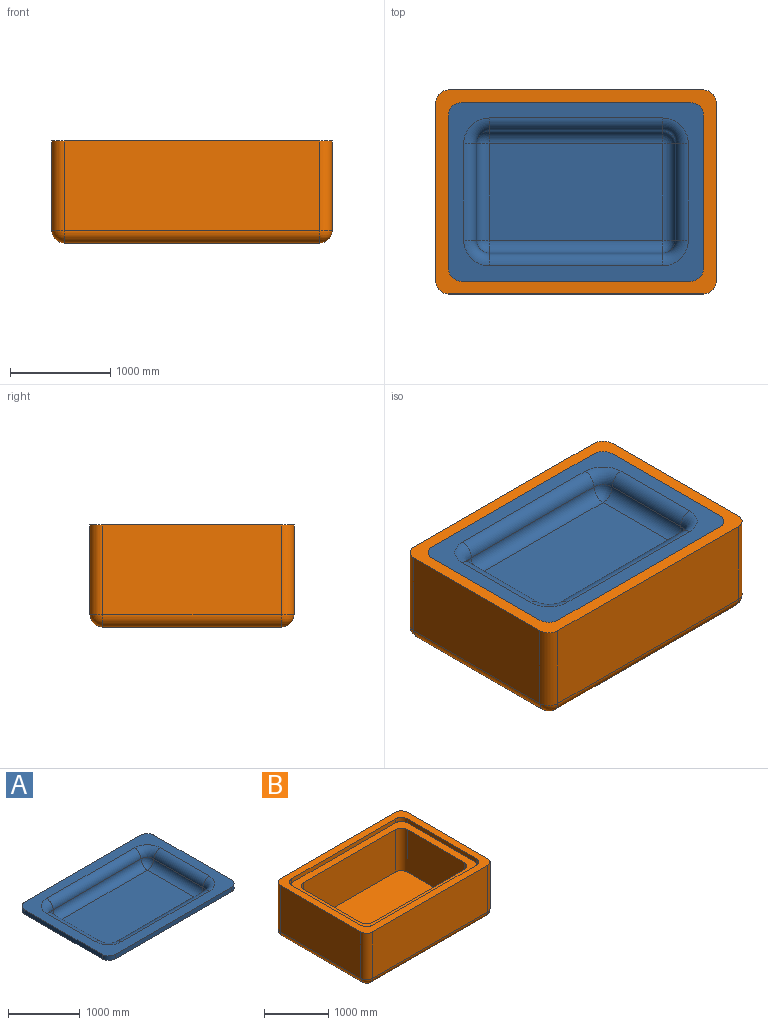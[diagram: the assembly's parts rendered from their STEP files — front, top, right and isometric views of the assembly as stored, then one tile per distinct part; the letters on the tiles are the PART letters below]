
ASSEMBLY  parts=2 mates=1
PART A: 52 faces, bbox 2540x1778x330.2 mm
  f0: plane 2540x1778mm, normal (0,0,1), area 1264759.1mm2, adj f1,f2,f3,f4,f13,f16,f17,f20
  f1: plane 2286x76.2mm, normal (0,1,0), area 174193.2mm2, adj f0,f5,f48,f51
  f2: plane 1524x76.2mm, normal (-1,0,0), area 116128.8mm2, adj f0,f5,f48,f49
  f3: plane 2286x76.2mm, normal (0,-1,0), area 174193.2mm2, adj f0,f5,f49,f50
  f4: plane 1524x76.2mm, normal (1,0,0), area 116128.8mm2, adj f0,f5,f50,f51
  f5: plane 2540x1778mm, normal (0,0,-1), area 1053854.6mm2, adj f1,f2,f3,f4,f40,f41,f42,f43
  f6: plane 1879.6x50.8mm, normal (0,-1,0), area 95483.7mm2, adj f30,f36,f39,f41
  f7: plane 1117.6x50.8mm, normal (-1,0,0), area 56774.1mm2, adj f33,f37,f39,f42
  f8: plane 1879.6x50.8mm, normal (0,1,0), area 95483.7mm2, adj f28,f32,f33,f46
  f9: plane 1117.6x50.8mm, normal (1,0,0), area 56774.1mm2, adj f28,f30,f31,f45
  f10: plane 1879.6x1117.6mm, normal (0,0,-1), area 2100641mm2, adj f31,f32,f36,f37
  f11: plane 1727.2x965.2mm, normal (0,0,1), area 1667093.4mm2, adj f14,f15,f22,f23
  f12: sphere r=127mm, area 25335.4mm2, adj f13,f14,f15
  f13: torus R=254mm, axis (0,0,1), area 54258.1mm2, adj f0,f12,f16,f17
  f14: cylinder r=127mm len=965.2mm, axis (0,1,0), area 192548.8mm2, adj f11,f12,f17,f18
  f15: cylinder r=127mm len=1727.2mm, axis (1,0,0), area 344561.1mm2, adj f11,f12,f16,f19
  f16: cylinder r=127mm len=1727.2mm, axis (-1,0,0), area 344561.1mm2, adj f0,f13,f15,f20
  f17: cylinder r=127mm len=965.2mm, axis (0,-1,0), area 192548.8mm2, adj f0,f13,f14,f21
  f18: sphere r=127mm, area 25335.4mm2, adj f14,f21,f22
  f19: sphere r=127mm, area 25335.4mm2, adj f15,f20,f23
  f20: torus R=254mm, axis (0,0,1), area 54258.1mm2, adj f0,f16,f19,f24
  f21: torus R=254mm, axis (0,0,1), area 54258.1mm2, adj f0,f17,f18,f25
  f22: cylinder r=127mm len=1727.2mm, axis (-1,0,0), area 344561.1mm2, adj f11,f18,f25,f26
  f23: cylinder r=127mm len=965.2mm, axis (0,-1,0), area 192548.8mm2, adj f11,f19,f24,f26
  f24: cylinder r=127mm len=965.2mm, axis (0,1,0), area 192548.8mm2, adj f0,f20,f23,f27
  f25: cylinder r=127mm len=1727.2mm, axis (1,0,0), area 344561.1mm2, adj f0,f21,f22,f27
  f26: sphere r=127mm, area 25335.4mm2, adj f22,f23,f27
  f27: torus R=254mm, axis (0,0,1), area 54258.1mm2, adj f0,f24,f25,f26
  f28: cylinder r=127mm len=127mm, axis (0,0,-1), area 10134.1mm2, adj f8,f9,f29,f47
  f29: sphere r=127mm, area 25335.4mm2, adj f28,f31,f32
  f30: cylinder r=127mm len=127mm, axis (0,0,1), area 10134.1mm2, adj f6,f9,f34,f43
  f31: cylinder r=127mm len=1117.6mm, axis (0,1,0), area 222951.3mm2, adj f9,f10,f29,f34
  f32: cylinder r=127mm len=1879.6mm, axis (-1,0,0), area 374963.5mm2, adj f8,f10,f29,f35
  f33: cylinder r=127mm len=127mm, axis (0,0,1), area 10134.1mm2, adj f7,f8,f35,f44
  f34: sphere r=127mm, area 25335.4mm2, adj f30,f31,f36
  f35: sphere r=127mm, area 25335.4mm2, adj f32,f33,f37
  f36: cylinder r=127mm len=1879.6mm, axis (1,0,0), area 374963.5mm2, adj f6,f10,f34,f38
  f37: cylinder r=127mm len=1117.6mm, axis (0,-1,0), area 222951.3mm2, adj f7,f10,f35,f38
  f38: sphere r=127mm, area 25335.4mm2, adj f36,f37,f39
  f39: cylinder r=127mm len=127mm, axis (0,0,-1), area 10134.1mm2, adj f6,f7,f38,f40
  f40: torus R=203.2mm, axis (0,0,1), area 29084.1mm2, adj f5,f39,f41,f42
  f41: cylinder r=76.2mm len=1879.6mm, axis (1,0,0), area 224978.1mm2, adj f5,f6,f40,f43
  f42: cylinder r=76.2mm len=1117.6mm, axis (0,-1,0), area 133770.8mm2, adj f5,f7,f40,f44
  f43: torus R=203.2mm, axis (0,0,1), area 29084.1mm2, adj f5,f30,f41,f45
  f44: torus R=203.2mm, axis (0,0,1), area 29084.1mm2, adj f5,f33,f42,f46
  f45: cylinder r=76.2mm len=1117.6mm, axis (0,1,0), area 133770.8mm2, adj f5,f9,f43,f47
  f46: cylinder r=76.2mm len=1879.6mm, axis (-1,0,0), area 224978.1mm2, adj f5,f8,f44,f47
  f47: torus R=203.2mm, axis (0,0,1), area 29084.1mm2, adj f5,f28,f45,f46
  f48: cylinder r=127mm len=127mm, axis (0,0,1), area 15201.2mm2, adj f0,f1,f2,f5
  f49: cylinder r=127mm len=127mm, axis (0,0,-1), area 15201.2mm2, adj f0,f2,f3,f5
  f50: cylinder r=127mm len=127mm, axis (0,0,1), area 15201.2mm2, adj f0,f3,f4,f5
  f51: cylinder r=127mm len=127mm, axis (0,0,-1), area 15201.2mm2, adj f0,f1,f4,f5
PART B: 36 faces, bbox 2794x2032x1016 mm
  f0: plane 2794x2032mm, normal (0,0,1), area 1161288mm2, adj f1,f2,f3,f4,f6,f7,f8,f9
  f1: plane 2540x889mm, normal (0,1,0), area 2258060mm2, adj f0,f21,f25,f27
  f2: plane 1778x889mm, normal (-1,0,0), area 1580642mm2, adj f0,f18,f24,f27
  f3: plane 2540x889mm, normal (0,-1,0), area 2258060mm2, adj f0,f16,f18,f19
  f4: plane 1778x889mm, normal (1,0,0), area 1580642mm2, adj f0,f16,f20,f21
  f5: plane 2540x1778mm, normal (0,0,-1), area 4516120mm2, adj f19,f20,f24,f25
  f6: plane 2286x76.2mm, normal (0,-1,0), area 174193.2mm2, adj f0,f10,f28,f31
  f7: plane 1524x76.2mm, normal (1,0,0), area 116128.8mm2, adj f0,f10,f28,f29
  f8: plane 2286x76.2mm, normal (0,1,0), area 174193.2mm2, adj f0,f10,f29,f30
  f9: plane 1524x76.2mm, normal (-1,0,0), area 116128.8mm2, adj f0,f10,f30,f31
  f10: plane 2540x1778mm, normal (0,0,1), area 1032256mm2, adj f6,f7,f8,f9,f12,f13,f14,f15
  f11: plane 2286x1524mm, normal (0,0,1), area 3470018.7mm2, adj f12,f13,f14,f15,f32,f33,f34,f35
  f12: plane 1270x812.8mm, normal (-1,0,0), area 1032256mm2, adj f10,f11,f34,f35
  f13: plane 2032x812.8mm, normal (0,1,0), area 1651609.6mm2, adj f10,f11,f33,f34
  f14: plane 1270x812.8mm, normal (1,0,0), area 1032256mm2, adj f10,f11,f32,f33
  f15: plane 2032x812.8mm, normal (0,-1,0), area 1651609.6mm2, adj f10,f11,f32,f35
  f16: cylinder r=127mm len=889mm, axis (0,0,1), area 177347.6mm2, adj f0,f3,f4,f17
  f17: sphere r=127mm, area 25335.4mm2, adj f16,f19,f20
  f18: cylinder r=127mm len=889mm, axis (0,0,-1), area 177347.6mm2, adj f0,f2,f3,f22
  f19: cylinder r=127mm len=2540mm, axis (1,0,0), area 506707.5mm2, adj f3,f5,f17,f22
  f20: cylinder r=127mm len=1778mm, axis (0,1,0), area 354695.2mm2, adj f4,f5,f17,f23
  f21: cylinder r=127mm len=889mm, axis (0,0,-1), area 177347.6mm2, adj f0,f1,f4,f23
  f22: sphere r=127mm, area 25335.4mm2, adj f18,f19,f24
  f23: sphere r=127mm, area 25335.4mm2, adj f20,f21,f25
  f24: cylinder r=127mm len=1778mm, axis (0,-1,0), area 354695.2mm2, adj f2,f5,f22,f26
  f25: cylinder r=127mm len=2540mm, axis (-1,0,0), area 506707.5mm2, adj f1,f5,f23,f26
  f26: sphere r=127mm, area 25335.4mm2, adj f24,f25,f27
  f27: cylinder r=127mm len=889mm, axis (0,0,1), area 177347.6mm2, adj f0,f1,f2,f26
  f28: cylinder r=127mm len=127mm, axis (0,0,1), area 15201.2mm2, adj f0,f6,f7,f10
  f29: cylinder r=127mm len=127mm, axis (0,0,-1), area 15201.2mm2, adj f0,f7,f8,f10
  f30: cylinder r=127mm len=127mm, axis (0,0,1), area 15201.2mm2, adj f0,f8,f9,f10
  f31: cylinder r=127mm len=127mm, axis (0,0,-1), area 15201.2mm2, adj f0,f6,f9,f10
  f32: cylinder r=127mm len=812.8mm, axis (0,0,1), area 162146.4mm2, adj f10,f11,f14,f15
  f33: cylinder r=127mm len=812.8mm, axis (0,0,-1), area 162146.4mm2, adj f10,f11,f13,f14
  f34: cylinder r=127mm len=812.8mm, axis (0,0,1), area 162146.4mm2, adj f10,f11,f12,f13
  f35: cylinder r=127mm len=812.8mm, axis (0,0,-1), area 162146.4mm2, adj f10,f11,f12,f15
PLACE A t=(1978.86,-1130.45,977.46)mm
PLACE B t=(1879.87,-1269.34,37.66)mm
MATE fastened B.f10 <-> A.f5  axis (0,0,1) through (700.18,-881.27,977.46)mm
